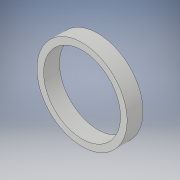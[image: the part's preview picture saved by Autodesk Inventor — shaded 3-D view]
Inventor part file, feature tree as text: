
AUTODESK INVENTOR PART (.ipt)
format: ipt  version: 2019 (Build 230136000, 136)  size: 104,960 bytes
history: native  units: mm
features: extrude x2, sketch x2
ambient origin geometry x8: Origin, YZ Plane, XZ Plane, XY Plane, X Axis, Y Axis, Z Axis, Center Point
bodies: Solid1 (feature_tree)
feature tree (4):
  extrude  "Extrusion1"  Depth=60.0mm TaperAngle=0.0deg
  extrude  "Extrusion2"  Depth=6.0mm TaperAngle=0.0deg
  sketch  "Sketch1"  dims[d0=340.0mm d1=60.0mm d2=0.0mm]
  sketch  "Sketch2"  dims[d3=290.0mm d4=6.0mm d5=0.0mm]
